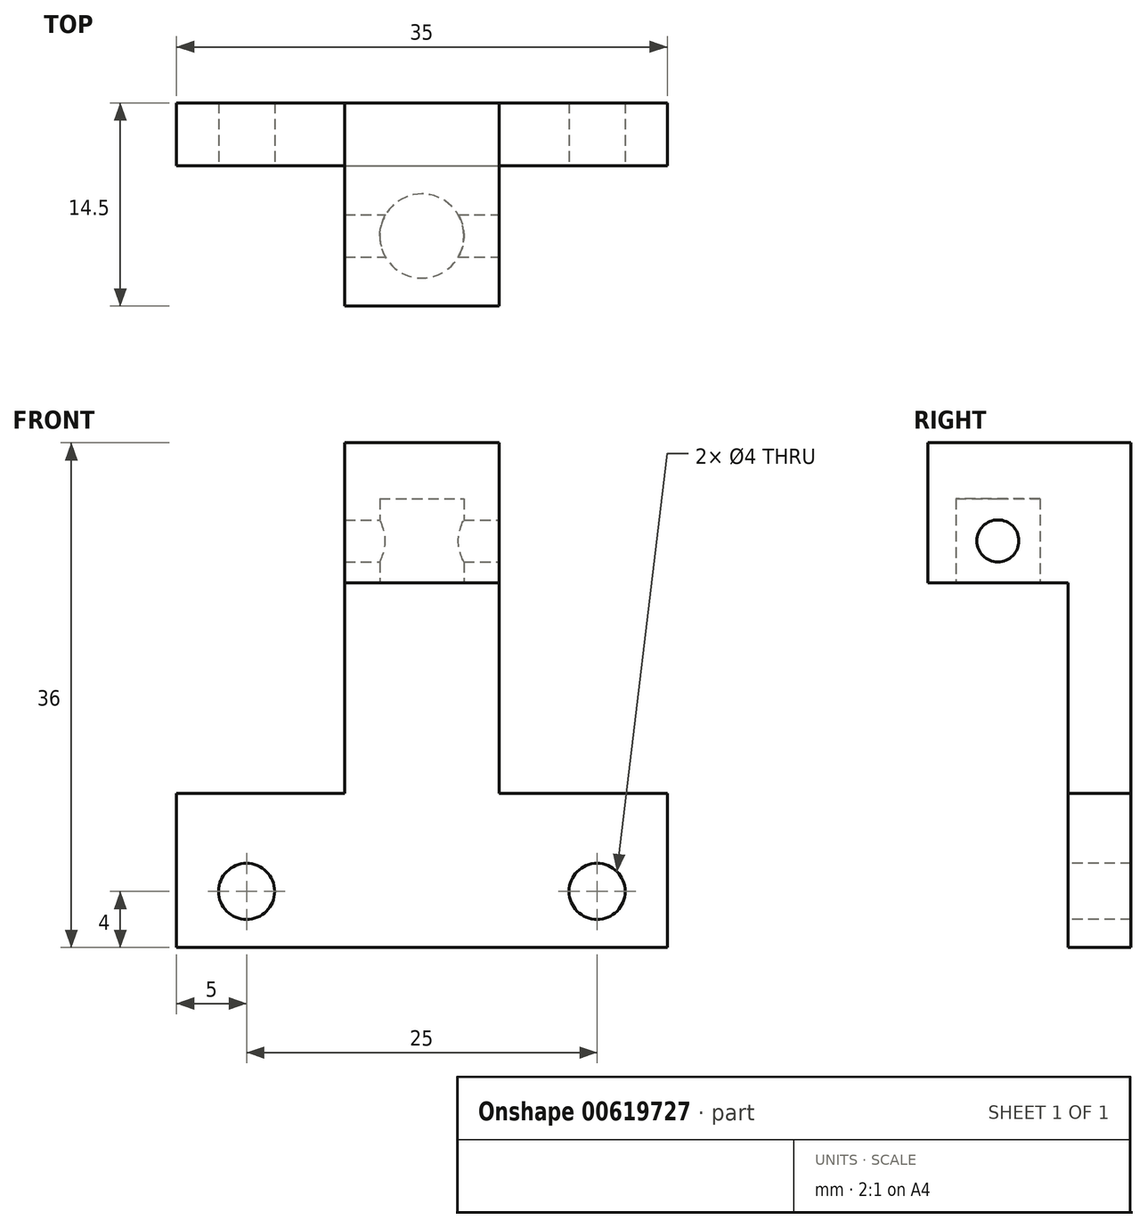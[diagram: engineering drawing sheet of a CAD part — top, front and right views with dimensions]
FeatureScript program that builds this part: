
annotation { "Feature Type Name" : "Feature", "Feature Type Description" : "" }
export const myFeature = defineFeature(function(context is Context, id is Id, definition is map)
    precondition{}
    {
        {
            var Q0;
            Q0=qCreatedBy(makeId("Front.planeOp"),FACE);
            var sketch = newSketch(context, id + "F0", { "sketchPlane" : qUnion([Q0])});
            skLineSegment(sketch, "E0.bottom", {"start": v(-17.5, 25) * mm, "end": v(17.5, 25) * mm});
            skLineSegment(sketch, "E0.top", {"start": v(-17.5, -20) * mm, "end": v(17.5, -20) * mm});
            skLineSegment(sketch, "E0.left", {"start": v(-17.5, 25) * mm, "end": v(-17.5, -20) * mm});
            skLineSegment(sketch, "E0.right", {"start": v(17.5, 25) * mm, "end": v(17.5, -20) * mm});
            skPoint(sketch, "E0.middle", {"position": v(0, 2.5) * mm});
            skSolve(sketch);
        }
        {
            var Q0;
            Q0=makeQuery(id+"F0.imprint","IMPRINT",FACE,{"disambiguationData":[TD([[makeQuery(id+"F0.imprint","IMPRINT",EDGE,{"derivedFrom":sQuery(id+"F0.wireOp",EDGE,"E0.bottom")}),-1.0]])]});
            extrude(context, id + "F1", {"entities" : qUnion([Q0]), "depth" : 4.5 * mm, "offsetDistance" : 25 * mm});
        }
        {
            var Q0;
            Q0=makeQuery(id+"F1.opExtrude","CAP_FACE",FACE,{"disambiguationData":[OSD([sQuery(id+"F0.wireOp",EDGE,"E0.bottom"),sQuery(id+"F0.wireOp",EDGE,"E0.top"),sQuery(id+"F0.wireOp",EDGE,"E0.left"),sQuery(id+"F0.wireOp",EDGE,"E0.right")])],"isStart":false});
            var sketch = newSketch(context, id + "F2", { "sketchPlane" : qUnion([Q0])});
            skCircle(sketch, "E1", {"center": v(12.5, -15) * mm, "radius": 2 * mm});
            skCircle(sketch, "E2.MirrorC", {"center": v(-12.5, -15) * mm, "radius": 2 * mm});
            skCircle(sketch, "E3.MirrorC", {"center": v(-12.5, -7) * mm, "radius": 2 * mm});
            skCircle(sketch, "E4.MirrorC", {"center": v(12.5, -7) * mm, "radius": 2 * mm});
            skSolve(sketch);
        }
        {
            var Q0;
            Q0=qSketchRegion(id+"F2",true);
            extrude(context, id + "F3", {"entities" : qUnion([Q0]), "operationType" : NewBodyOperationType.REMOVE, "oppositeDirection" : true, "depth" : 10 * mm, "offsetDistance" : 25 * mm});
        }
        {
            var Q0;
            Q0=makeQuery(id+"F1.opExtrude","CAP_FACE",FACE,{"disambiguationData":[OSD([sQuery(id+"F0.wireOp",EDGE,"E0.bottom"),sQuery(id+"F0.wireOp",EDGE,"E0.top"),sQuery(id+"F0.wireOp",EDGE,"E0.left"),sQuery(id+"F0.wireOp",EDGE,"E0.right")])],"isStart":false});
            var sketch = newSketch(context, id + "F4", { "sketchPlane" : qUnion([Q0])});
            skLineSegment(sketch, "E5.bottom", {"start": v(-17.5, 25) * mm, "end": v(17.5, 25) * mm});
            skLineSegment(sketch, "E5.top", {"start": v(-17.5, 15) * mm, "end": v(17.5, 15) * mm});
            skLineSegment(sketch, "E5.left", {"start": v(-17.5, 25) * mm, "end": v(-17.5, 15) * mm});
            skLineSegment(sketch, "E5.right", {"start": v(17.5, 25) * mm, "end": v(17.5, 15) * mm});
            skSolve(sketch);
        }
        {
            var Q0;
            Q0 = qSketchRegion(id + "F4", true);
            extrude(context, id + "F5", {"entities" : qUnion([Q0]), "operationType" : NewBodyOperationType.ADD, "depth" : 10 * mm, "offsetDistance" : 25 * mm});
        }
        {
            var Q0;
            Q0=makeQuery(id+"F5.opExtrude","SWEPT_FACE",FACE,{"disambiguationData":[OSD([sQuery(id+"F4.wireOp",EDGE,"E5.top")])]});
            var sketch = newSketch(context, id + "F6", { "sketchPlane" : qUnion([Q0])});
            skCircle(sketch, "E6", {"center": v(0, 9.5) * mm, "radius": 3 * mm});
            skPoint(sketch, "E6.centerSnap0", {"position": v(17.5, 9.5) * mm});
            skPoint(sketch, "E6.centerSnap1", {"position": v(0, 14.5) * mm});
            skSolve(sketch);
        }
        {
            var Q0;
            Q0 = qSketchRegion(id + "F6", true);
            extrude(context, id + "F7", {"entities" : qUnion([Q0]), "operationType" : NewBodyOperationType.REMOVE, "oppositeDirection" : true, "depth" : 6 * mm, "offsetDistance" : 25 * mm});
        }
        {
            var Q0;
            Q0=makeQuery(id+"F1.opExtrude","SWEPT_FACE",FACE,{"disambiguationData":[OSD([sQuery(id+"F0.wireOp",EDGE,"E0.top")])]});
            var sketch = newSketch(context, id + "F8", { "sketchPlane" : qUnion([Q0])});
            skLineSegment(sketch, "E7.0.0", {"start": v(-17.5, 0) * mm, "end": v(17.5, 0) * mm});
            skLineSegment(sketch, "E7.0.1", {"start": v(17.5, 0) * mm, "end": v(17.5, 4.5) * mm});
            skLineSegment(sketch, "E7.0.2", {"start": v(17.5, 4.5) * mm, "end": v(-17.5, 4.5) * mm});
            skLineSegment(sketch, "E7.0.3", {"start": v(-17.5, 4.5) * mm, "end": v(-17.5, 0) * mm});
            skSolve(sketch);
        }
        {
            var Q0;
            Q0 = qSketchRegion(id + "F8", true);
            extrude(context, id + "F9", {"entities" : qUnion([Q0]), "operationType" : NewBodyOperationType.REMOVE, "oppositeDirection" : true, "depth" : 2 * mm, "offsetDistance" : 25 * mm});
        }
        {
            var Q0;
            Q0=makeQuery(id+"F5.opExtrude","CAP_FACE",FACE,{"disambiguationData":[OSD([sQuery(id+"F4.wireOp",EDGE,"E5.bottom"),sQuery(id+"F4.wireOp",EDGE,"E5.top"),sQuery(id+"F4.wireOp",EDGE,"E5.left"),sQuery(id+"F4.wireOp",EDGE,"E5.right")])],"isStart":false});
            var sketch = newSketch(context, id + "F10", { "sketchPlane" : qUnion([Q0])});
            skLineSegment(sketch, "E8.bottom", {"start": v(-17.5, 25) * mm, "end": v(-5.5, 25) * mm});
            skLineSegment(sketch, "E8.top", {"start": v(-17.5, 0) * mm, "end": v(-5.5, 0) * mm});
            skLineSegment(sketch, "E8.left", {"start": v(-17.5, 25) * mm, "end": v(-17.5, 0) * mm});
            skLineSegment(sketch, "E8.right", {"start": v(-5.5, 25) * mm, "end": v(-5.5, 0) * mm});
            skLineSegment(sketch, "E9.MirrorCS", {"start": v(17.5, 25) * mm, "end": v(5.5, 25) * mm});
            skLineSegment(sketch, "E10.MirrorCS", {"start": v(5.5, 25) * mm, "end": v(5.5, 0) * mm});
            skLineSegment(sketch, "E11.MirrorCS", {"start": v(17.5, 0) * mm, "end": v(5.5, 0) * mm});
            skLineSegment(sketch, "E12.MirrorCS", {"start": v(17.5, 25) * mm, "end": v(17.5, 0) * mm});
            skSolve(sketch);
        }
        {
            var Q0;
            Q0 = qSketchRegion(id + "F10", true);
            extrude(context, id + "F11", {"entities" : qUnion([Q0]), "operationType" : NewBodyOperationType.REMOVE, "endBound" : BoundingType.THROUGH_ALL, "oppositeDirection" : true, "depth" : 25 * mm, "offsetDistance" : 25 * mm});
        }
        {
            var Q0;
            Q0=makeQuery(id+"F11.boolean.opBoolean","COPY",FACE,{"derivedFrom":makeQuery(id+"F11.opExtrude","SWEPT_FACE",FACE,{"disambiguationData":[OSD([sQuery(id+"F10.wireOp",EDGE,"E10.MirrorCS")])]})});
            var sketch = newSketch(context, id + "F12", { "sketchPlane" : qUnion([Q0])});
            skCircle(sketch, "E13", {"center": v(-9.5, 18) * mm, "radius": 1.5 * mm});
            skSolve(sketch);
        }
        {
            var Q0;
            Q0 = qSketchRegion(id + "F12", true);
            extrude(context, id + "F13", {"entities" : qUnion([Q0]), "operationType" : NewBodyOperationType.REMOVE, "endBound" : BoundingType.THROUGH_ALL, "oppositeDirection" : true, "depth" : 25 * mm, "offsetDistance" : 25 * mm});
        }
        {
            var Q0;
            Q0=makeQuery(id+"F1.opExtrude","CAP_FACE",FACE,{"disambiguationData":[OSD([sQuery(id+"F0.wireOp",EDGE,"E0.bottom"),sQuery(id+"F0.wireOp",EDGE,"E0.top"),sQuery(id+"F0.wireOp",EDGE,"E0.left"),sQuery(id+"F0.wireOp",EDGE,"E0.right")])],"isStart":false});
            var sketch = newSketch(context, id + "F14", { "sketchPlane" : qUnion([Q0])});
            skLineSegment(sketch, "E14.bottom", {"start": v(-17.5, -18) * mm, "end": v(17.5, -18) * mm});
            skLineSegment(sketch, "E14.top", {"start": v(-17.5, -12) * mm, "end": v(17.5, -12) * mm});
            skLineSegment(sketch, "E14.left", {"start": v(-17.5, -18) * mm, "end": v(-17.5, -12) * mm});
            skLineSegment(sketch, "E14.right", {"start": v(17.5, -18) * mm, "end": v(17.5, -12) * mm});
            skSolve(sketch);
        }
        {
            var Q0;
            Q0 = qSketchRegion(id + "F14", true);
            extrude(context, id + "F15", {"entities" : qUnion([Q0]), "operationType" : NewBodyOperationType.REMOVE, "endBound" : BoundingType.THROUGH_ALL, "oppositeDirection" : true, "depth" : 25 * mm, "offsetDistance" : 25 * mm});
        }
        {
            var Q0;
            Q0=makeQuery(id+"F15.boolean.opBoolean","COPY",FACE,{"derivedFrom":makeQuery(id+"F15.opExtrude","SWEPT_FACE",FACE,{"disambiguationData":[OSD([sQuery(id+"F14.wireOp",EDGE,"E14.top")])]})});
            var sketch = newSketch(context, id + "F16", { "sketchPlane" : qUnion([Q0])});
            skLineSegment(sketch, "E15.0.0", {"start": v(-17.5, 0) * mm, "end": v(17.5, 0) * mm});
            skLineSegment(sketch, "E15.0.1", {"start": v(17.5, 0) * mm, "end": v(17.5, 4.5) * mm});
            skLineSegment(sketch, "E15.0.2", {"start": v(17.5, 4.5) * mm, "end": v(-17.5, 4.5) * mm});
            skLineSegment(sketch, "E15.0.3", {"start": v(-17.5, 4.5) * mm, "end": v(-17.5, 0) * mm});
            skSolve(sketch);
        }
        {
            var Q0;
            Q0 = qSketchRegion(id + "F16", true);
            extrude(context, id + "F17", {"entities" : qUnion([Q0]), "operationType" : NewBodyOperationType.REMOVE, "oppositeDirection" : true, "depth" : 1 * mm, "offsetDistance" : 25 * mm});
        }
    });
